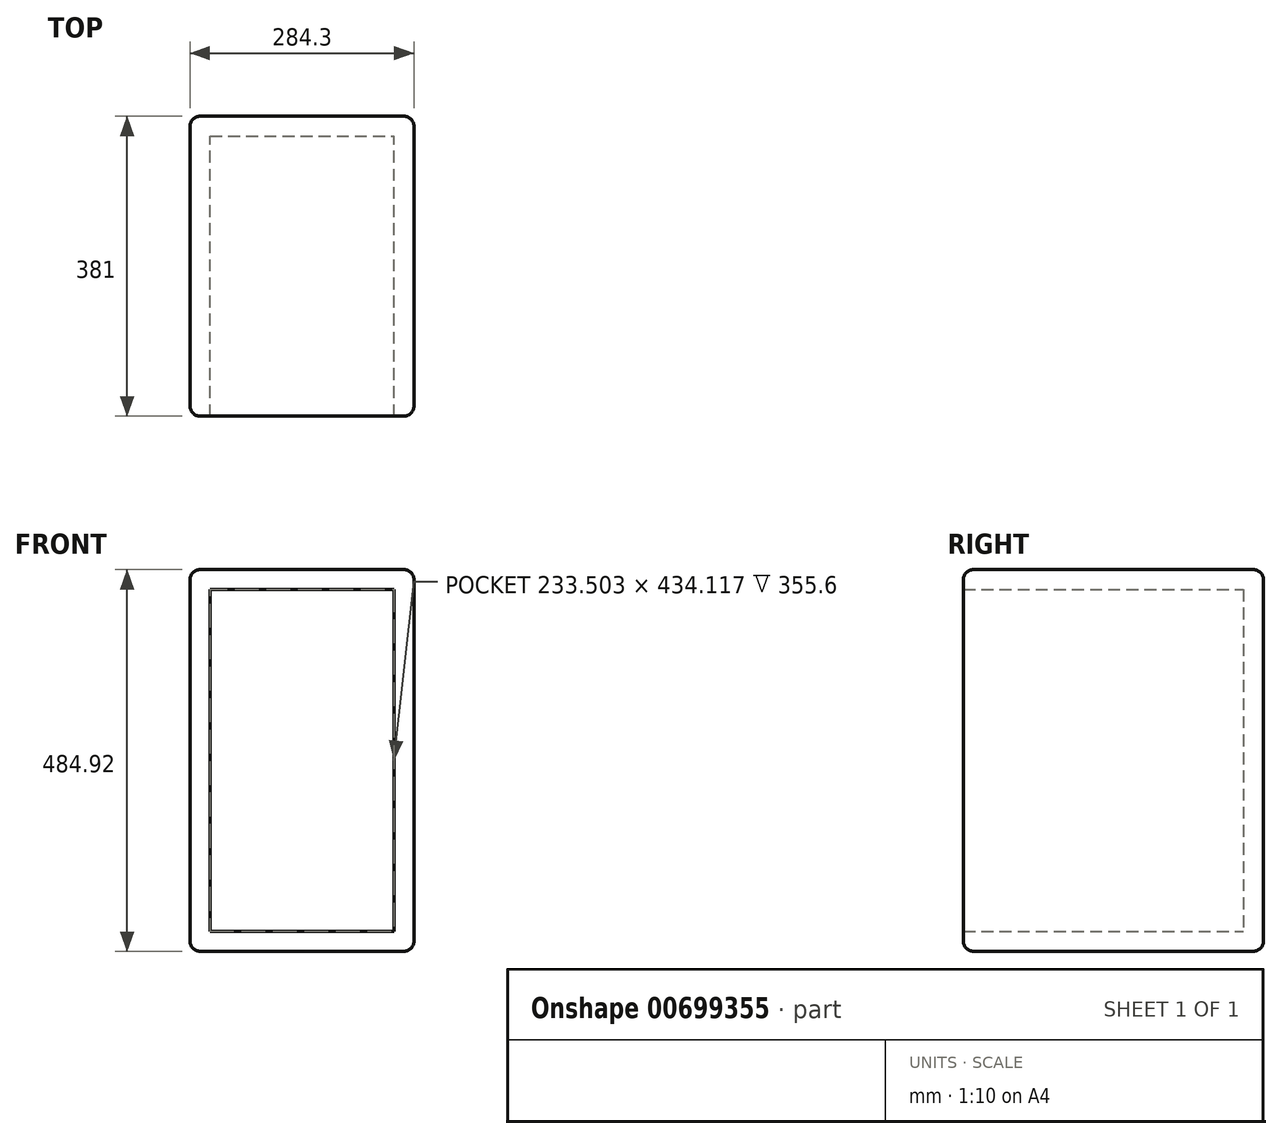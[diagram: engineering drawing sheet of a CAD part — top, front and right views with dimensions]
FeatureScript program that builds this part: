
annotation { "Feature Type Name" : "Feature", "Feature Type Description" : "" }
export const myFeature = defineFeature(function(context is Context, id is Id, definition is map)
    precondition{}
    {
        {
            var Q0;
            Q0=qCreatedBy(makeId("Front.planeOp"),FACE);
            var sketch = newSketch(context, id + "F0", { "sketchPlane" : qUnion([Q0])});
            skLineSegment(sketch, "E0.bottom", {"start": v(142.15, -242.46) * mm, "end": v(-142.15, -242.46) * mm});
            skLineSegment(sketch, "E0.top", {"start": v(142.15, 242.46) * mm, "end": v(-142.15, 242.46) * mm});
            skLineSegment(sketch, "E0.left", {"start": v(142.15, -242.46) * mm, "end": v(142.15, 242.46) * mm});
            skLineSegment(sketch, "E0.right", {"start": v(-142.15, -242.46) * mm, "end": v(-142.15, 242.46) * mm});
            skPoint(sketch, "E0.middle", {"position": v(0, 0) * mm});
            skSolve(sketch);
        }
        {
            var Q0;
            Q0=makeQuery(id+"F0.imprint","IMPRINT",FACE,{"disambiguationData":[TD([[makeQuery(id+"F0.imprint","IMPRINT",EDGE,{"derivedFrom":sQuery(id+"F0.wireOp",EDGE,"E0.bottom")}),-1.0]])]});
            extrude(context, id + "F1", {"entities" : qUnion([Q0]), "depth" : 381 * mm, "offsetDistance" : 25.4 * mm});
        }
        {
            var Q0;
            Q0=makeQuery(id+"F1.opExtrude","CAP_EDGE",EDGE,{"disambiguationData":[OSD([sQuery(id+"F0.wireOp",EDGE,"E0.left")])],"isStart":false});
            fillet(context, id + "F2", {"entities" : qUnion([Q0]), "radius" : 12.7 * mm, "tangentPropagation" : true, "allowEdgeOverflow" : false});
        }
        {
            var Q0;
            Q0=makeQuery(id+"F1.opExtrude","CAP_EDGE",EDGE,{"disambiguationData":[OSD([sQuery(id+"F0.wireOp",EDGE,"E0.top")])],"isStart":false});
            var Q1;
            Q1=makeQuery(id+"F1.opExtrude","CAP_EDGE",EDGE,{"disambiguationData":[OSD([sQuery(id+"F0.wireOp",EDGE,"E0.right")])],"isStart":false});
            fillet(context, id + "F3", {"entities" : qUnion([Q0, Q1]), "radius" : 12.7 * mm, "tangentPropagation" : true, "allowEdgeOverflow" : false});
        }
        {
            var Q0;
            Q0=makeQuery(id+"F1.opExtrude","CAP_EDGE",EDGE,{"disambiguationData":[OSD([sQuery(id+"F0.wireOp",EDGE,"E0.left")])],"isStart":true});
            fillet(context, id + "F4", {"entities" : qUnion([Q0]), "radius" : 12.7 * mm, "tangentPropagation" : true, "allowEdgeOverflow" : false});
        }
        {
            var Q0;
            Q0=makeQuery(id+"F1.opExtrude","CAP_EDGE",EDGE,{"disambiguationData":[OSD([sQuery(id+"F0.wireOp",EDGE,"E0.right")])],"isStart":true});
            fillet(context, id + "F5", {"entities" : qUnion([Q0]), "radius" : 12.7 * mm, "tangentPropagation" : true, "allowEdgeOverflow" : false});
        }
        {
            var Q0;
            Q0=makeQuery(id+"F1.opExtrude","SWEPT_EDGE",EDGE,{"disambiguationData":[OSD([sQuery(id+"F0.wireOp",EDGE,"E0.bottom"),sQuery(id+"F0.wireOp",EDGE,"E0.right")])]});
            fillet(context, id + "F6", {"entities" : qUnion([Q0]), "radius" : 12.7 * mm, "tangentPropagation" : true, "allowEdgeOverflow" : false});
        }
        {
            var Q0;
            Q0=makeQuery(id+"F1.opExtrude","CAP_FACE",FACE,{"disambiguationData":[OSD([sQuery(id+"F0.wireOp",EDGE,"E0.bottom"),sQuery(id+"F0.wireOp",EDGE,"E0.top"),sQuery(id+"F0.wireOp",EDGE,"E0.left"),sQuery(id+"F0.wireOp",EDGE,"E0.right")])],"isStart":false});
            shell(context, id + "F7", {"entities" : qUnion([Q0]), "thickness" : 25.4 * mm});
        }
    });
